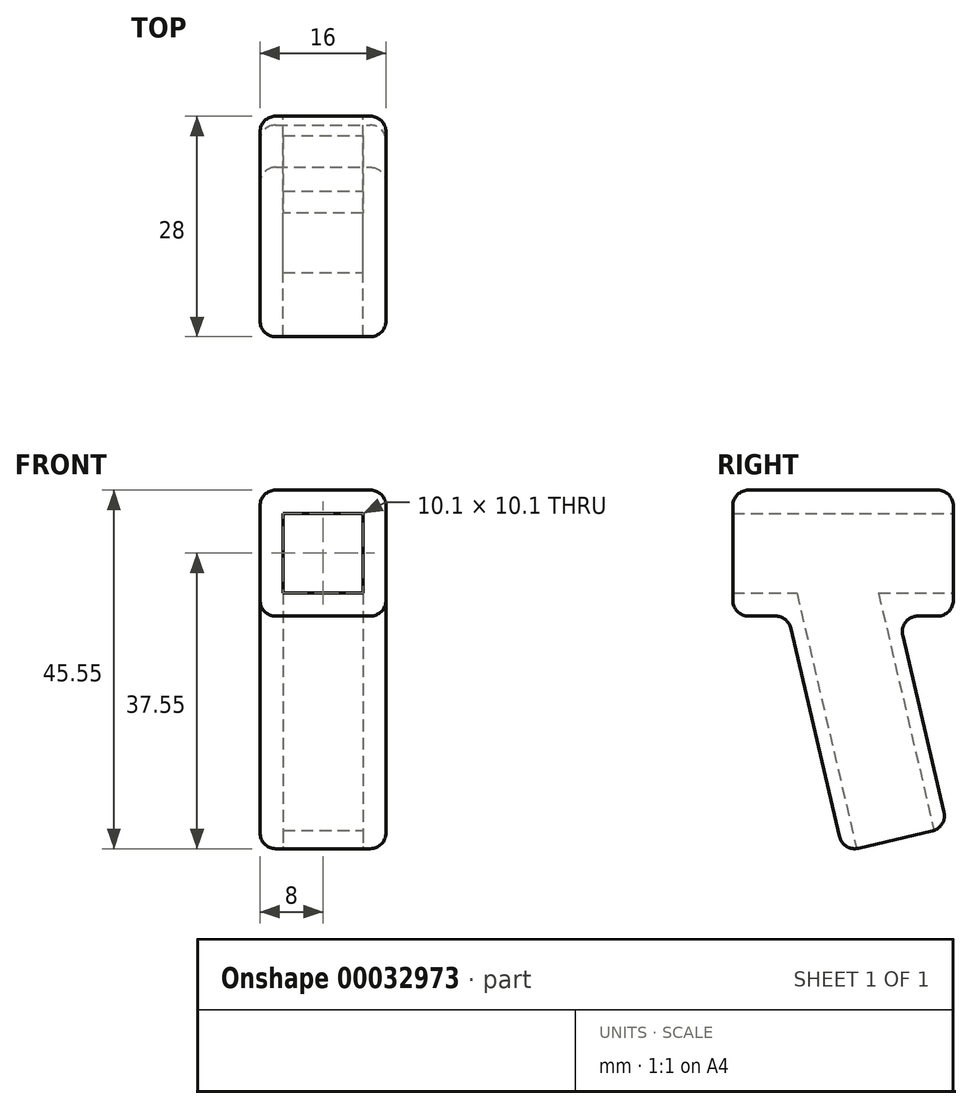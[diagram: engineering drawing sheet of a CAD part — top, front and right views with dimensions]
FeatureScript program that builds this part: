
annotation { "Feature Type Name" : "Feature", "Feature Type Description" : "" }
export const myFeature = defineFeature(function(context is Context, id is Id, definition is map)
    precondition{}
    {
        {
            var Q0;
            Q0=qCreatedBy(makeId("Right.planeOp"),FACE);
            var sketch = newSketch(context, id + "F0", { "sketchPlane" : qUnion([Q0])});
            skLineSegment(sketch, "E0.rect.bottom", {"start": v(14, -8) * mm, "end": v(7, -8) * mm});
            skLineSegment(sketch, "E0.rect.top", {"start": v(14, 8) * mm, "end": v(-14, 8) * mm});
            skLineSegment(sketch, "E0.rect.left", {"start": v(14, -8) * mm, "end": v(14, 8) * mm});
            skLineSegment(sketch, "E0.rect.right", {"start": v(-14, -8) * mm, "end": v(-14, 8) * mm});
            skPoint(sketch, "E0.rect.middle", {"position": v(0, 0) * mm});
            skLineSegment(sketch, "E1.rect.bottom", {"start": v(7, -8) * mm, "end": v(-7, -8) * mm, "construction": true});
            skLineSegment(sketch, "E1.rect.top", {"start": v(7, 8) * mm, "end": v(-7, 8) * mm, "construction": true});
            skLineSegment(sketch, "E1.rect.left", {"start": v(7, -8) * mm, "end": v(7, 8) * mm, "construction": true});
            skLineSegment(sketch, "E1.rect.right", {"start": v(-7, -8) * mm, "end": v(-7, 8) * mm, "construction": true});
            skLineSegment(sketch, "E2", {"start": v(-7, -8) * mm, "end": v(0, -37.95) * mm});
            skLineSegment(sketch, "E3", {"start": v(7, -8) * mm, "end": v(13.27, -34.85) * mm});
            skLineSegment(sketch, "E4.trimOffspring", {"start": v(-7, -8) * mm, "end": v(-14, -8) * mm});
            skLineSegment(sketch, "E5", {"start": v(0, -37.95) * mm, "end": v(13.27, -34.85) * mm});
            skPoint(sketch, "E6.orphan", {"position": v(14, -37.95) * mm});
            skSolve(sketch);
        }
        {
            var Q0;
            Q0 = qSketchRegion(id + "F0", true);
            extrude(context, id + "F1", {"entities" : qUnion([Q0]), "depth" : 16 * mm, "symmetric" : true});
        }
        {
            var Q0;
            Q0=makeQuery(id+"F1.opExtrude","SWEPT_FACE",FACE,{"disambiguationData":[OSD([sQuery(id+"F0.wireOp",EDGE,"E0.rect.left")])]});
            var sketch = newSketch(context, id + "F2", { "sketchPlane" : qUnion([Q0])});
            skLineSegment(sketch, "E7.rect.bottom", {"start": v(5.05, -5.05) * mm, "end": v(-5.05, -5.05) * mm});
            skLineSegment(sketch, "E7.rect.top", {"start": v(5.05, 5.05) * mm, "end": v(-5.05, 5.05) * mm});
            skLineSegment(sketch, "E7.rect.left", {"start": v(5.05, -5.05) * mm, "end": v(5.05, 5.05) * mm});
            skLineSegment(sketch, "E7.rect.right", {"start": v(-5.05, -5.05) * mm, "end": v(-5.05, 5.05) * mm});
            skPoint(sketch, "E7.rect.middle", {"position": v(0, 0) * mm});
            skSolve(sketch);
        }
        {
            var Q0;
            Q0 = qSketchRegion(id + "F2", true);
            extrude(context, id + "F3", {"entities" : qUnion([Q0]), "operationType" : NewBodyOperationType.REMOVE, "endBound" : BoundingType.UP_TO_NEXT, "oppositeDirection" : true, "depth" : 25 * mm});
        }
        {
            var Q0;
            Q0=makeQuery(id+"F1.opExtrude","SWEPT_FACE",FACE,{"disambiguationData":[OSD([sQuery(id+"F0.wireOp",EDGE,"E5")])]});
            var sketch = newSketch(context, id + "F4", { "sketchPlane" : qUnion([Q0])});
            skLineSegment(sketch, "E8", {"start": v(8, 8.64) * mm, "end": v(-8, -5) * mm, "construction": true});
            skLineSegment(sketch, "E9", {"start": v(-8, -5) * mm, "end": v(8, -5) * mm, "construction": true});
            skLineSegment(sketch, "E10", {"start": v(8, -5) * mm, "end": v(-8, 8.64) * mm, "construction": true});
            skLineSegment(sketch, "E11.rect.bottom", {"start": v(-5.05, -3.23) * mm, "end": v(5.05, -3.23) * mm});
            skLineSegment(sketch, "E11.rect.top", {"start": v(-5.05, 6.87) * mm, "end": v(5.05, 6.87) * mm});
            skLineSegment(sketch, "E11.rect.left", {"start": v(-5.05, -3.23) * mm, "end": v(-5.05, 6.87) * mm});
            skLineSegment(sketch, "E11.rect.right", {"start": v(5.05, -3.23) * mm, "end": v(5.05, 6.87) * mm});
            skPoint(sketch, "E11.rect.middle", {"position": v(0, 1.82) * mm});
            skSolve(sketch);
        }
        {
            var Q0;
            Q0 = qSketchRegion(id + "F4", true);
            extrude(context, id + "F5", {"entities" : qUnion([Q0]), "operationType" : NewBodyOperationType.REMOVE, "endBound" : BoundingType.UP_TO_NEXT, "oppositeDirection" : true, "depth" : 25 * mm});
        }
        {
            var Q0;
            Q0=makeQuery(id+"F1.opExtrude","SWEPT_FACE",FACE,{"disambiguationData":[OSD([sQuery(id+"F0.wireOp",EDGE,"E0.rect.top")])]});
            var Q1;
            Q1=makeQuery(id+"F1.opExtrude","CAP_FACE",FACE,{"disambiguationData":[OSD([sQuery(id+"F0.wireOp",EDGE,"E0.rect.bottom"),sQuery(id+"F0.wireOp",EDGE,"E0.rect.top"),sQuery(id+"F0.wireOp",EDGE,"E0.rect.left"),sQuery(id+"F0.wireOp",EDGE,"E0.rect.right"),sQuery(id+"F0.wireOp",EDGE,"E2"),sQuery(id+"F0.wireOp",EDGE,"E3"),sQuery(id+"F0.wireOp",EDGE,"E4.trimOffspring"),sQuery(id+"F0.wireOp",EDGE,"E5")])],"isStart":true});
            var Q2;
            Q2=makeQuery(id+"F1.opExtrude","SWEPT_FACE",FACE,{"disambiguationData":[OSD([sQuery(id+"F0.wireOp",EDGE,"E2")])]});
            var Q3;
            Q3=makeQuery(id+"F1.opExtrude","CAP_FACE",FACE,{"disambiguationData":[OSD([sQuery(id+"F0.wireOp",EDGE,"E0.rect.bottom"),sQuery(id+"F0.wireOp",EDGE,"E0.rect.top"),sQuery(id+"F0.wireOp",EDGE,"E0.rect.left"),sQuery(id+"F0.wireOp",EDGE,"E0.rect.right"),sQuery(id+"F0.wireOp",EDGE,"E2"),sQuery(id+"F0.wireOp",EDGE,"E3"),sQuery(id+"F0.wireOp",EDGE,"E4.trimOffspring"),sQuery(id+"F0.wireOp",EDGE,"E5")])],"isStart":false});
            var Q4;
            Q4=makeQuery(id+"F1.opExtrude","SWEPT_FACE",FACE,{"disambiguationData":[OSD([sQuery(id+"F0.wireOp",EDGE,"E3")])]});
            var Q5;
            Q5=makeQuery(id+"F1.opExtrude","SWEPT_FACE",FACE,{"disambiguationData":[OSD([sQuery(id+"F0.wireOp",EDGE,"E0.rect.bottom")])]});
            var Q6;
            Q6=makeQuery(id+"F1.opExtrude","SWEPT_FACE",FACE,{"disambiguationData":[OSD([sQuery(id+"F0.wireOp",EDGE,"E4.trimOffspring")])]});
            fillet(context, id + "F6", {"entities" : qUnion([Q0, Q1, Q2, Q3, Q4, Q5, Q6]), "radius" : 2 * mm, "tangentPropagation" : true, "allowEdgeOverflow" : false});
        }
    });
